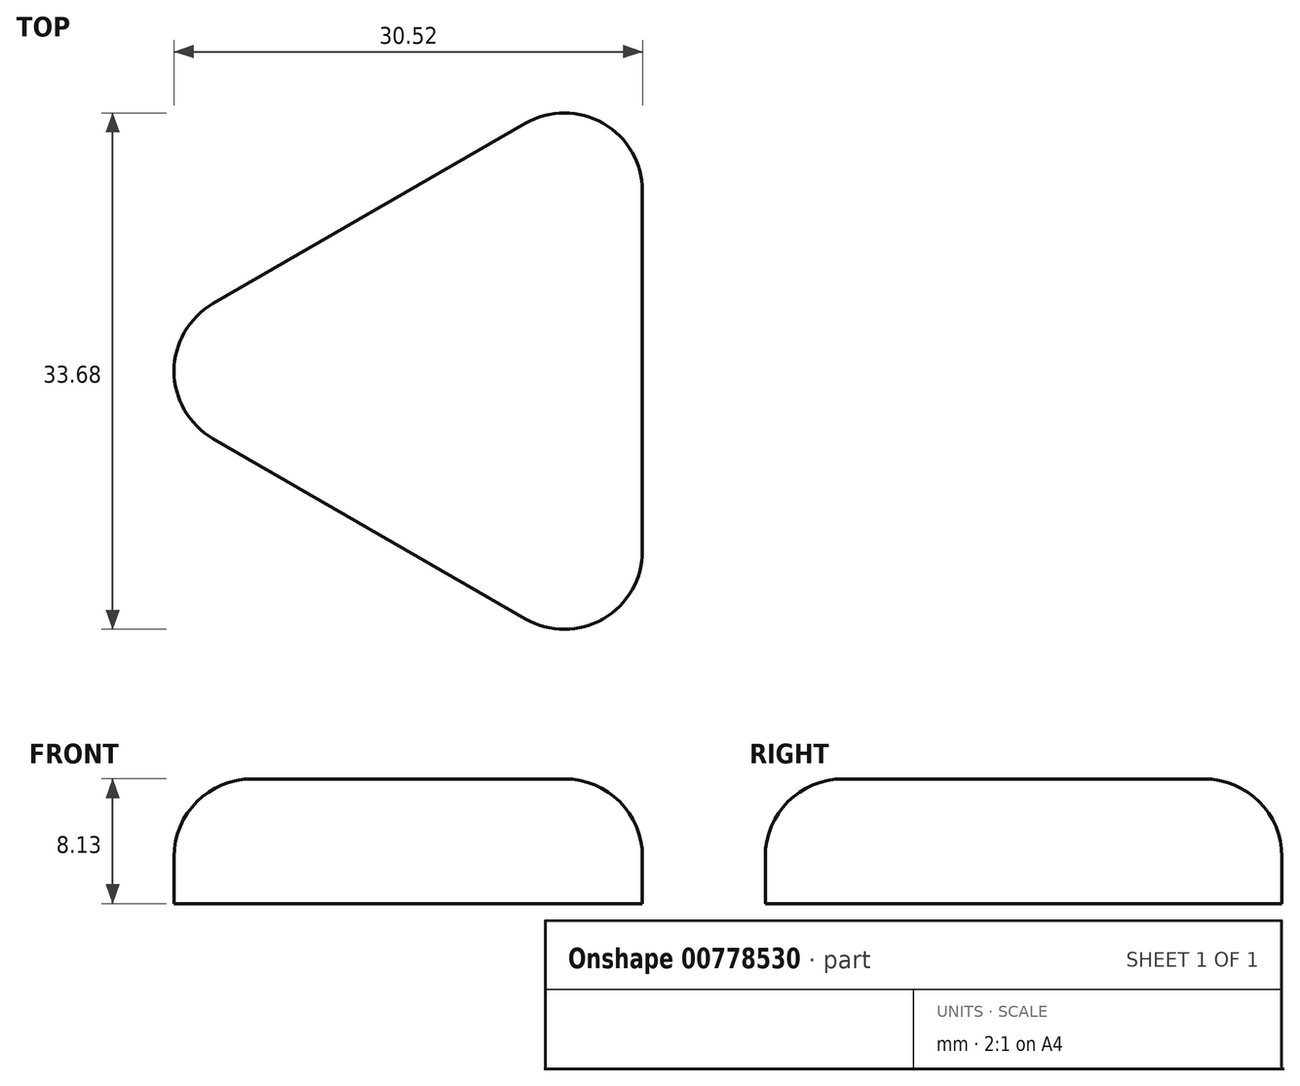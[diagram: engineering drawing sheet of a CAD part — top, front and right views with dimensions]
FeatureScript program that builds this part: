
annotation { "Feature Type Name" : "Feature", "Feature Type Description" : "" }
export const myFeature = defineFeature(function(context is Context, id is Id, definition is map)
    precondition{}
    {
        {
            var Q0;
            Q0=qCreatedBy(makeId("Top.planeOp"),FACE);
            var sketch = newSketch(context, id + "F0", { "sketchPlane" : qUnion([Q0])});
            skCircle(sketch, "E0.cCircle", {"center": v(0, 0) * mm, "radius": 11.87 * mm, "construction": true});
            skLineSegment(sketch, "E0.0", {"start": v(11.87, 20.55) * mm, "end": v(11.87, -20.55) * mm});
            skLineSegment(sketch, "E0.1", {"start": v(11.87, -20.55) * mm, "end": v(-23.73, 0) * mm});
            skLineSegment(sketch, "E0.2", {"start": v(-23.73, 0) * mm, "end": v(11.87, 20.55) * mm});
            skPoint(sketch, "E0.0.midPoint", {"position": v(11.87, 0) * mm});
            skSolve(sketch);
        }
        {
            var Q0;
            Q0=makeQuery(id+"F0.imprint","IMPRINT",FACE,{"disambiguationData":[TD([[makeQuery(id+"F0.imprint","IMPRINT",EDGE,{"derivedFrom":sQuery(id+"F0.wireOp",EDGE,"E0.0")}),-1.0]])]});
            extrude(context, id + "F1", {"entities" : qUnion([Q0]), "depth" : 8.13 * mm, "offsetDistance" : 25.4 * mm});
        }
        {
            var Q0;
            Q0=makeQuery(id+"F1.opExtrude","SWEPT_EDGE",EDGE,{"disambiguationData":[OSD([sQuery(id+"F0.wireOp",EDGE,"E0.0"),sQuery(id+"F0.wireOp",EDGE,"E0.1")])]});
            var Q1;
            Q1=makeQuery(id+"F1.opExtrude","SWEPT_EDGE",EDGE,{"disambiguationData":[OSD([sQuery(id+"F0.wireOp",EDGE,"E0.1"),sQuery(id+"F0.wireOp",EDGE,"E0.2")])]});
            var Q2;
            Q2=makeQuery(id+"F1.opExtrude","SWEPT_EDGE",EDGE,{"disambiguationData":[OSD([sQuery(id+"F0.wireOp",EDGE,"E0.0"),sQuery(id+"F0.wireOp",EDGE,"E0.2")])]});
            fillet(context, id + "F2", {"entities" : qUnion([Q0, Q1, Q2]), "radius" : 5.08 * mm, "tangentPropagation" : true, "allowEdgeOverflow" : false});
        }
        {
            var Q0;
            Q0=makeQuery(id+"F1.opExtrude","CAP_EDGE",EDGE,{"disambiguationData":[OSD([sQuery(id+"F0.wireOp",EDGE,"E0.0")])],"isStart":false});
            fillet(context, id + "F3", {"entities" : qUnion([Q0]), "radius" : 5.08 * mm, "tangentPropagation" : true, "allowEdgeOverflow" : false});
        }
    });
